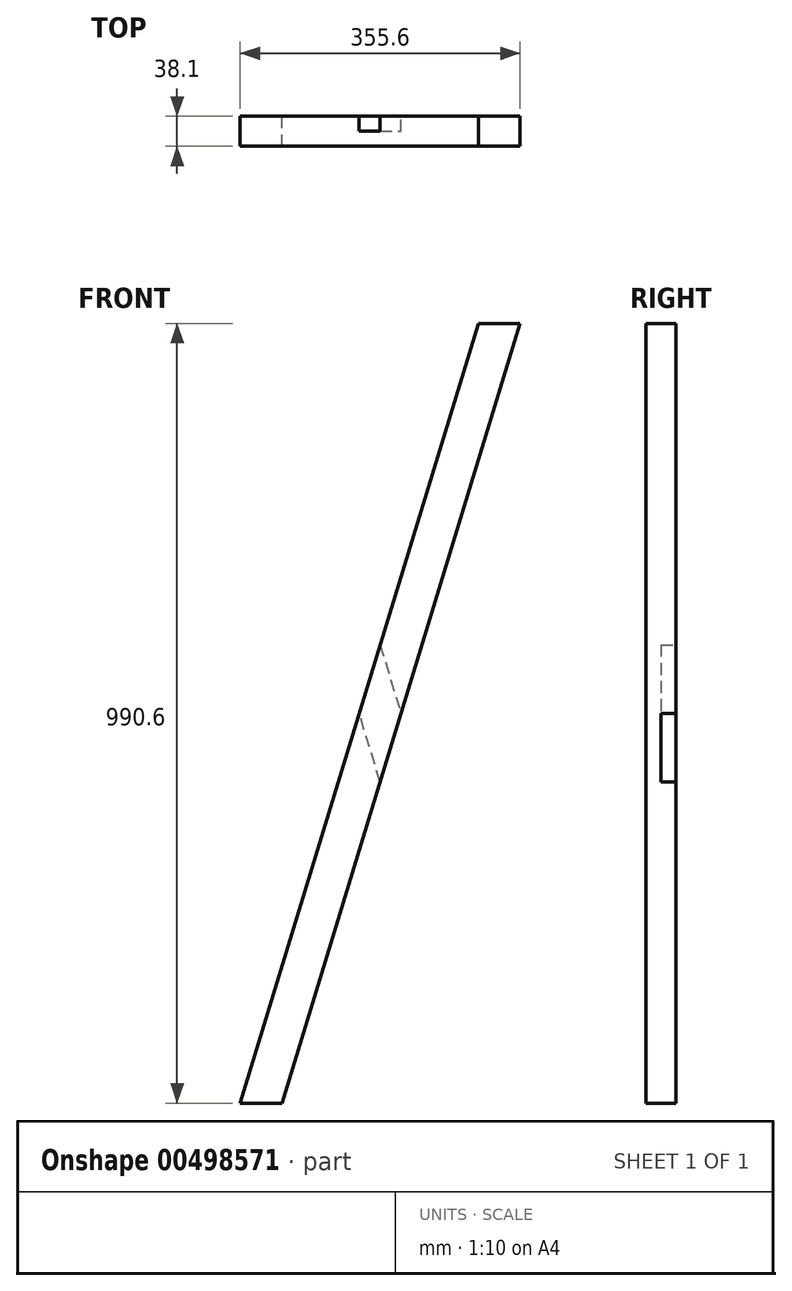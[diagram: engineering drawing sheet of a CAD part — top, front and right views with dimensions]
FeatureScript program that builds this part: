
annotation { "Feature Type Name" : "Feature", "Feature Type Description" : "" }
export const myFeature = defineFeature(function(context is Context, id is Id, definition is map)
    precondition{}
    {
        {
            var Q0;
            Q0=qCreatedBy(makeId("Front.planeOp"),FACE);
            var sketch = newSketch(context, id + "F0", { "sketchPlane" : qUnion([Q0])});
            skLineSegment(sketch, "E0", {"start": v(0, 0) * mm, "end": v(53.12, 0) * mm});
            skLineSegment(sketch, "E1", {"start": v(53.12, 0) * mm, "end": v(355.6, 990.6) * mm});
            skLineSegment(sketch, "E2", {"start": v(355.6, 990.6) * mm, "end": v(302.48, 990.6) * mm});
            skLineSegment(sketch, "E3", {"start": v(302.48, 990.6) * mm, "end": v(0, 0) * mm});
            skSolve(sketch);
        }
        {
            var Q0;
            Q0 = qSketchRegion(id + "F0", true);
            extrude(context, id + "F1", {"entities" : qUnion([Q0]), "depth" : 38.1 * mm});
        }
        {
            var Q0;
            Q0=makeQuery(id+"F1.opExtrude","CAP_FACE",FACE,{"disambiguationData":[OSD([sQuery(id+"F0.wireOp",EDGE,"E0"),sQuery(id+"F0.wireOp",EDGE,"E1"),sQuery(id+"F0.wireOp",EDGE,"E2"),sQuery(id+"F0.wireOp",EDGE,"E3")])],"isStart":true});
            var sketch = newSketch(context, id + "F2", { "sketchPlane" : qUnion([Q0])});
            skLineSegment(sketch, "E4", {"start": v(-177.8, 408.32) * mm, "end": v(-151.24, 495.3) * mm});
            skLineSegment(sketch, "E5", {"start": v(-151.24, 495.3) * mm, "end": v(-177.8, 582.27) * mm});
            skLineSegment(sketch, "E6", {"start": v(-177.8, 582.27) * mm, "end": v(-204.36, 495.3) * mm});
            skLineSegment(sketch, "E7", {"start": v(-204.36, 495.3) * mm, "end": v(-177.8, 408.32) * mm});
            skSolve(sketch);
        }
        {
            var Q0;
            Q0 = qSketchRegion(id + "F2", true);
            extrude(context, id + "F3", {"entities" : qUnion([Q0]), "operationType" : NewBodyOperationType.REMOVE, "oppositeDirection" : true, "depth" : 19.05 * mm});
        }
    });
